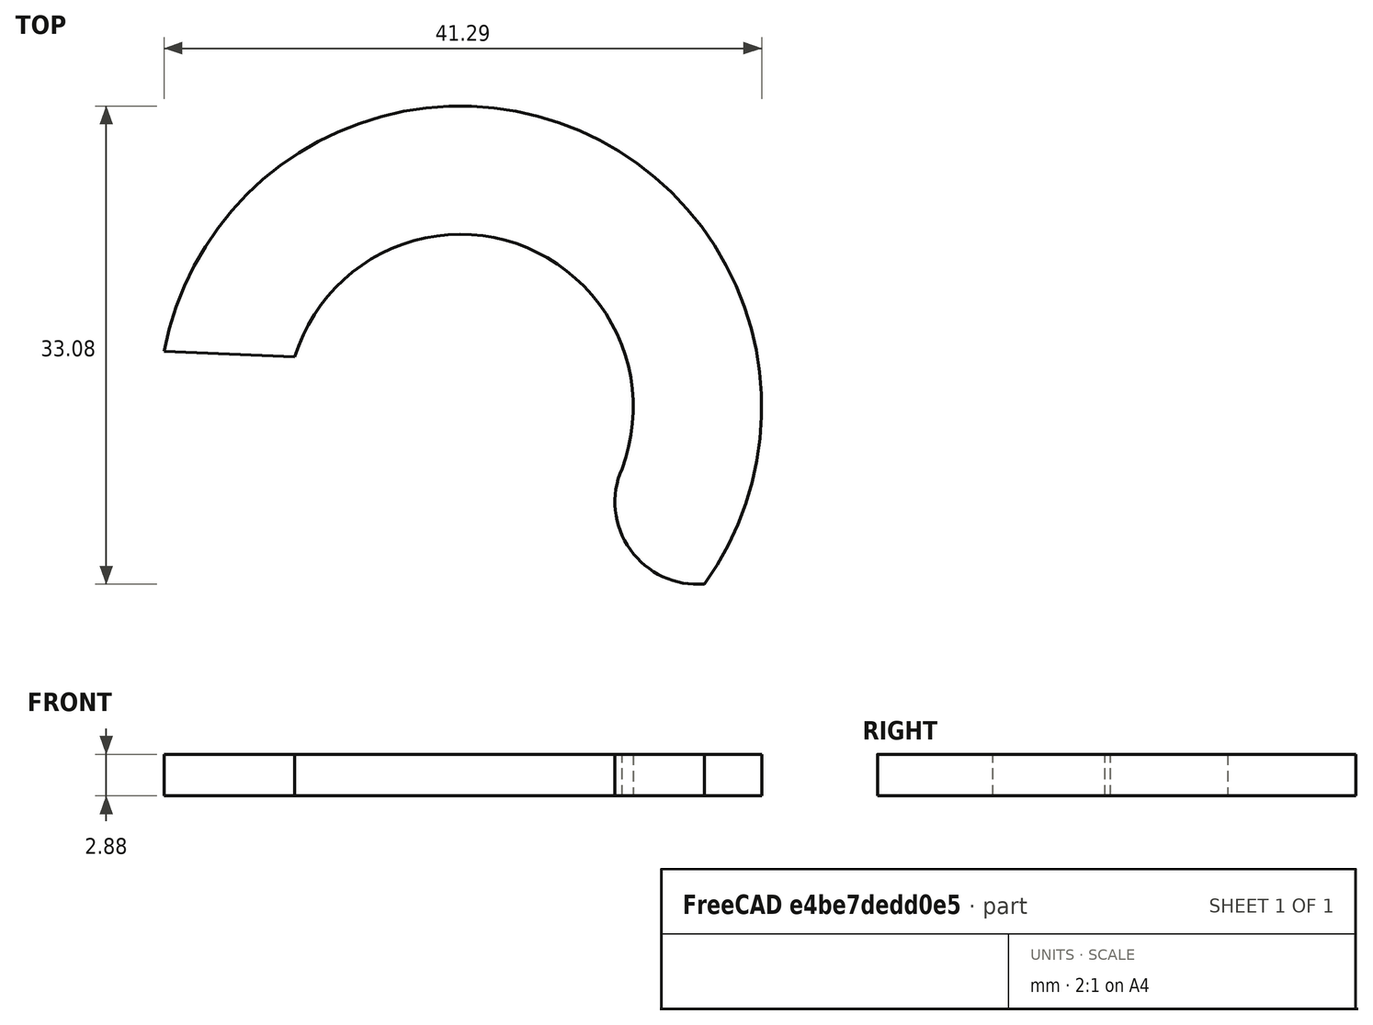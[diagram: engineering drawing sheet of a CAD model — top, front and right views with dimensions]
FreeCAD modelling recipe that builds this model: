
FCSTD DOCUMENT  (FreeCAD 1.0R39109 (Git))
Label: latch
License: All rights reserved
LicenseURL: https://en.wikipedia.org/wiki/All_rights_reserved
objects: Mesh::Feature×1, Sketcher::SketchObject×1, PartDesign::Pad×1, PartDesign::Body×1, App::Part×1
note: 6 computed .brp shape members not serialized (recipe doc carries the construction recipe); baked Part::Feature solids carry a one-line shape summary decoded from their .brp

FEATURE [Mesh::Feature] Servo_Arm
FEATURE [Sketcher::SketchObject] Sketch
  ArcFitTolerance = 1e-06
  AttachmentSupport = -> [XY_Plane001]
  FullyConstrained = false
  MakeInternals = false
  MapMode = 5
  sketch-geometry (4):
    g0: ArcOfCircle CenterX=27.0336 CenterY=0 CenterZ=0 NormalX=0 NormalY=0 NormalZ=1 AngleXU=0 Radius=20.829 StartAngle=5.65582 EndAngle=9.23784
    g1: ArcOfCircle CenterX=27.0336 CenterY=0 CenterZ=0 NormalX=0 NormalY=0 NormalZ=1 AngleXU=0 Radius=11.9562 StartAngle=5.91932 EndAngle=9.12918
    g2: ArcOfCircle CenterX=43.4171 CenterY=-6.55283 CenterZ=0 NormalX=0 NormalY=0 NormalZ=1 AngleXU=0 Radius=5.69426 StartAngle=2.72623 EndAngle=4.79665
    g3: LineSegment StartX=6.56746 StartY=3.87105 StartZ=0 EndX=15.596 EndY=3.48303 EndZ=0
  constraints (6):
    c: PointOnObject(g0,g-1)
    c: Coincident(g1,g0)
    c: Coincident(g2,g0)
    c: Coincident(g2,g1)
    c: Coincident(g3,g0)
    c: Coincident(g3,g1)
FEATURE [PartDesign::Pad] Pad
  Direction = (0,0,1)
  Length = 2.88
  Length2 = 10
  Profile = -> Sketch
  ReferenceAxis = -> Sketch [N_Axis]
  Refine = true
  Suppressed = false
  Type = 0
FEATURE [PartDesign::Body] Body
  AllowCompound = false
  Group = -> [Sketch,Pad]
  Origin = -> Origin001
  Tip = -> Pad
FEATURE [App::Part] Part
  Group = -> [Body]
  Origin = -> Origin
